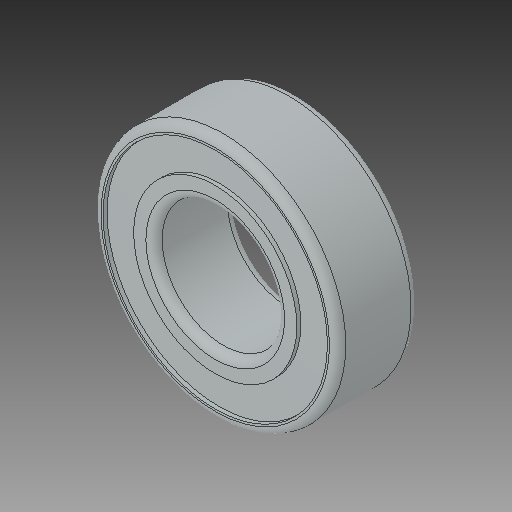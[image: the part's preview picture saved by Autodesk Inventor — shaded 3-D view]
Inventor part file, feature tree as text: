
AUTODESK INVENTOR PART (.ipt)
format: ipt  version: 2019.4 (Build 234330000, 330)  size: 175,104 bytes
history: mixed  units: mm
features: fillet x1, imported_body x1
ambient origin geometry x8: Origin, YZ Plane, XZ Plane, XY Plane, X Axis, Y Axis, Z Axis, Center Point
bodies: Solid1 (imported_parasolid)
feature tree (2):
  fillet  "Fillet1"  [1 undecoded]
  imported_body  NMx_Import_Brep_tag  [imported B-rep: ~16 faces, bbox_mm=[3.0, 0.0, 4.0]]
note: 1 required parameter value undecoded (feature->parameter linkage not recoverable at this tier; creation-order binding heuristic only, values carry confidence <= 0.55)
